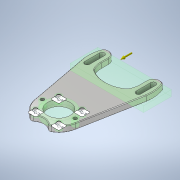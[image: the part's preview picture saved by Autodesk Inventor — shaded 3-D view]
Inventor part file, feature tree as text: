
AUTODESK INVENTOR PART (.ipt)
format: ipt  version: 2020.1 (Build 241239000, 239)  size: 564,736 bytes
history: native  units: mm
features: thread x6, emboss x2, fillet x2, extrude x1, chamfer x1, other x1, sketch x1
ambient origin geometry x8: Origin, YZ Plane, XZ Plane, XY Plane, X Axis, Y Axis, Z Axis, Center Point
bodies: Body1 (feature_tree)
feature tree (14):
  extrude  "Extrusion3"  Depth=19.0mm
  thread  "Thread1"  [1 undecoded]
  thread  "Thread2"  [1 undecoded]
  thread  "Thread4"  [1 undecoded]
  thread  "Thread5"  [1 undecoded]
  thread  "Thread6"  [1 undecoded]
  thread  "Thread7"  [1 undecoded]
  emboss  "Emboss1"
  emboss  "Emboss2"
  fillet  "Fillet3"  Radius=3.0mm
  fillet  "Fillet5"  Radius=3.0mm
  chamfer  "Chamfer3"  Angle=45.0deg  [1 undecoded]
  other  "Center Lines"
  sketch  "Sketch1"  dims[d0=51.5mm d1=19.0mm d3=3.5mm d4=3.5mm d5=7.0mm d9=3.5mm d11=32.0mm d15=4.1mm d24=3.0mm d25=3.0mm d27=45.0deg d29=3.0mm d30=3.0mm d40=5.0mm d41=0.0mm d44=10.0mm d45=0.0mm d46=10.0mm d47=0.0mm d50=15.0mm d51=52.0mm d53=27.0mm d54=10.0mm d55=0.0mm d56=10.0mm d57=0.0mm d58=10.0mm d59=0.0mm d60=10.0mm d61=0.0mm d65=0.5mm d66=0.0mm d73=0.5mm d74=0.0mm d75=80.75mm d76=8.0mm d78=0.0mm d81=6.25mm d82=12.5mm d85=5.0mm d86=4.0mm d91=0.5mm d94=2.0mm d95=0.5mm d96=2.0mm d97=45.0deg d98=15.0deg d99=24.0mm d101=43.0mm d104=2.0mm d105=27.5mm]
note: 7 required parameter values undecoded (feature->parameter linkage not recoverable at this tier; creation-order binding heuristic only, values carry confidence <= 0.55)
